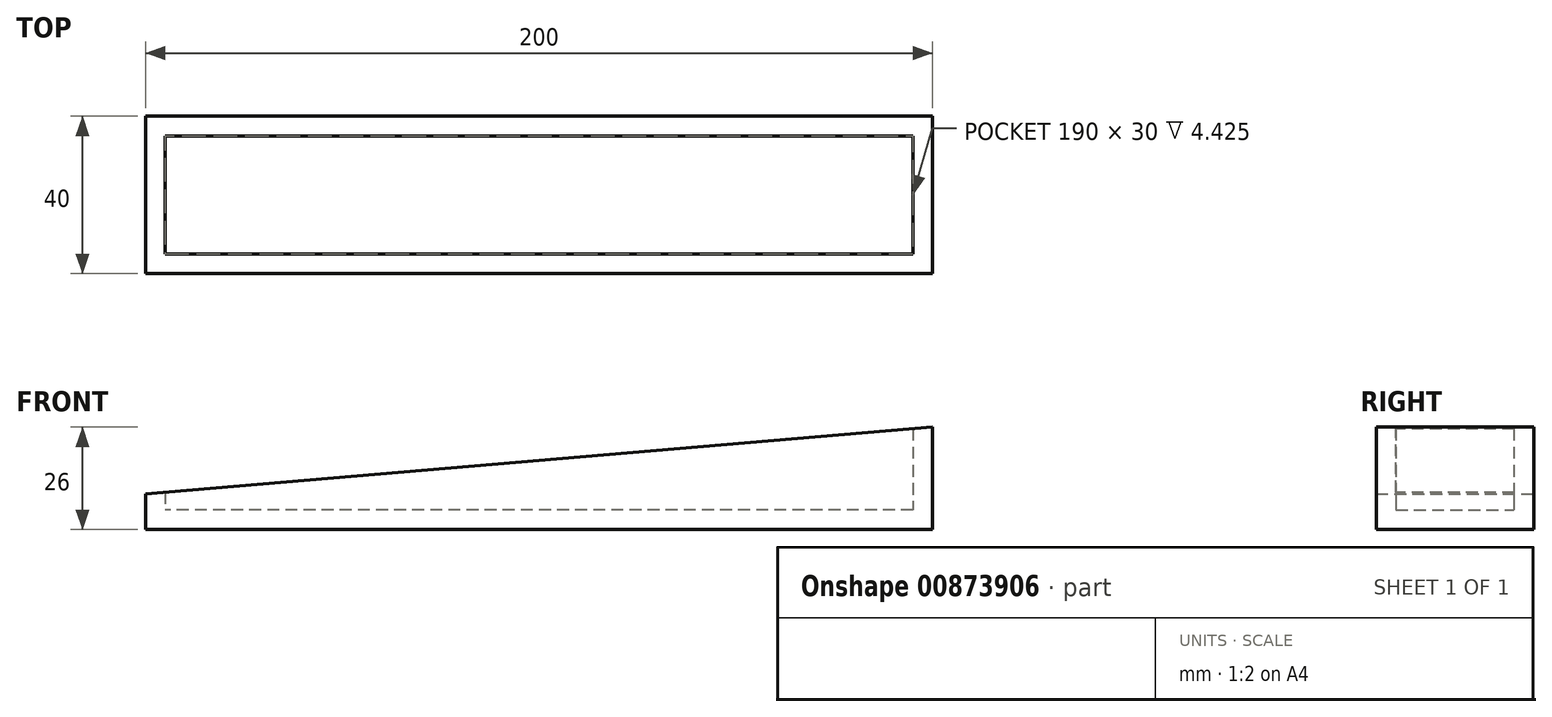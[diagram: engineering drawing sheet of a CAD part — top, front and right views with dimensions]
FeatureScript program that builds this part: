
annotation { "Feature Type Name" : "Feature", "Feature Type Description" : "" }
export const myFeature = defineFeature(function(context is Context, id is Id, definition is map)
    precondition{}
    {
        {
            var Q0;
            Q0=qCreatedBy(makeId("Top.planeOp"),FACE);
            var sketch = newSketch(context, id + "F0", { "sketchPlane" : qUnion([Q0])});
            skLineSegment(sketch, "E0.bottom", {"start": v(100, -20) * mm, "end": v(-100, -20) * mm});
            skLineSegment(sketch, "E0.top", {"start": v(100, 20) * mm, "end": v(-100, 20) * mm});
            skLineSegment(sketch, "E0.left", {"start": v(100, -20) * mm, "end": v(100, 20) * mm});
            skLineSegment(sketch, "E0.right", {"start": v(-100, -20) * mm, "end": v(-100, 20) * mm});
            skPoint(sketch, "E0.middle", {"position": v(0, 0) * mm});
            skSolve(sketch);
        }
        {
            var Q0;
            Q0 = qSketchRegion(id + "F0", true);
            extrude(context, id + "F1", {"entities" : qUnion([Q0]), "depth" : 26 * mm, "offsetDistance" : 25 * mm});
        }
        {
            var Q0;
            Q0=makeQuery(id+"F1.opExtrude","CAP_EDGE",EDGE,{"disambiguationData":[OSD([sQuery(id+"F0.wireOp",EDGE,"E0.right")])],"isStart":false});
            chamfer(context, id + "F2", {"entities" : qUnion([Q0]), "chamferType" : ChamferType.TWO_OFFSETS, "width1" : 17 * mm, "oppositeDirection" : false, "width2" : 200 * mm, "tangentPropagation" : true});
        }
        {
            var Q0;
            Q0=makeQuery(id+"F2.opChamfer","BLEND_FACE",FACE,{"disambiguationData":[OSD([sQuery(id+"F0.wireOp",EDGE,"E0.right")])]});
            shell(context, id + "F3", {"entities" : qUnion([Q0]), "thickness" : 5 * mm});
        }
    });
